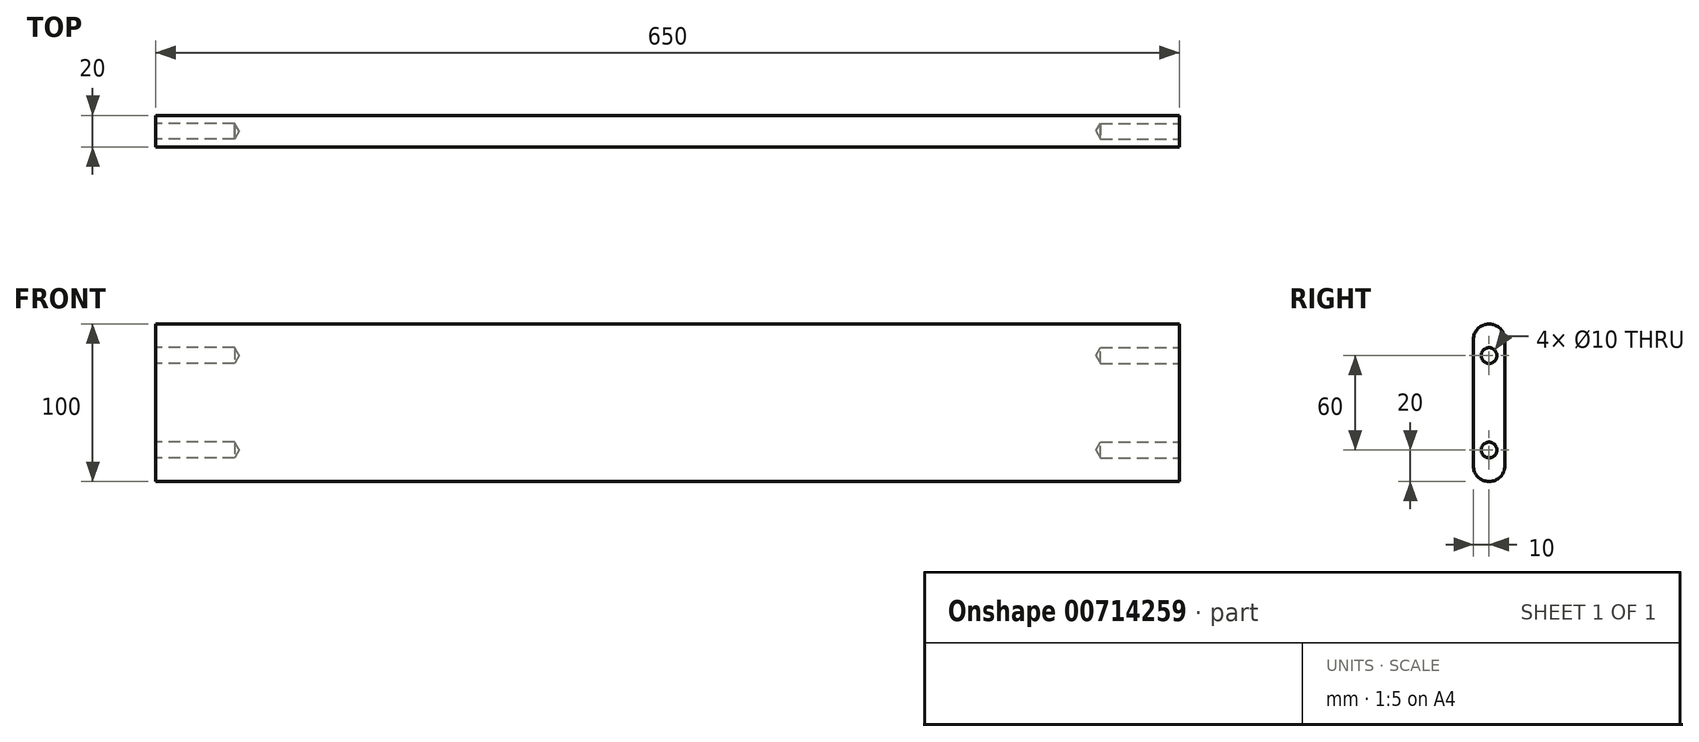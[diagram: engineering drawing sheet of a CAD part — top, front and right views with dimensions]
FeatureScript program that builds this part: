
annotation { "Feature Type Name" : "Feature", "Feature Type Description" : "" }
export const myFeature = defineFeature(function(context is Context, id is Id, definition is map)
    precondition{}
    {
        {
            var Q0;
            Q0=qCreatedBy(makeId("Front.planeOp"),FACE);
            var sketch = newSketch(context, id + "F0", { "sketchPlane" : qUnion([Q0])});
            skLineSegment(sketch, "E0.bottom", {"start": v(0, 0) * mm, "end": v(-650, 0) * mm});
            skLineSegment(sketch, "E0.top", {"start": v(0, 100) * mm, "end": v(-650, 100) * mm});
            skLineSegment(sketch, "E0.left", {"start": v(0, 0) * mm, "end": v(0, 100) * mm});
            skLineSegment(sketch, "E0.right", {"start": v(-650, 0) * mm, "end": v(-650, 100) * mm});
            skSolve(sketch);
        }
        {
            var Q0;
            Q0=makeQuery(id+"F0.imprint","IMPRINT",FACE,{"disambiguationData":[TD([[makeQuery(id+"F0.imprint","IMPRINT",EDGE,{"derivedFrom":sQuery(id+"F0.wireOp",EDGE,"E0.bottom")}),-1.0]])]});
            extrude(context, id + "F1", {"entities" : qUnion([Q0]), "depth" : 20 * mm, "offsetDistance" : 25 * mm});
        }
        {
            var Q0;
            Q0=makeQuery(id+"F1.opExtrude","CAP_EDGE",EDGE,{"disambiguationData":[OSD([sQuery(id+"F0.wireOp",EDGE,"E0.top")])],"isStart":true});
            var Q1;
            Q1=makeQuery(id+"F1.opExtrude","CAP_EDGE",EDGE,{"disambiguationData":[OSD([sQuery(id+"F0.wireOp",EDGE,"E0.top")])],"isStart":false});
            var Q2;
            Q2=makeQuery(id+"F1.opExtrude","CAP_EDGE",EDGE,{"disambiguationData":[OSD([sQuery(id+"F0.wireOp",EDGE,"E0.bottom")])],"isStart":true});
            var Q3;
            Q3=makeQuery(id+"F1.opExtrude","CAP_EDGE",EDGE,{"disambiguationData":[OSD([sQuery(id+"F0.wireOp",EDGE,"E0.bottom")])],"isStart":false});
            fillet(context, id + "F2", {"entities" : qUnion([Q0, Q1, Q2, Q3]), "radius" : 10 * mm, "tangentPropagation" : true, "allowEdgeOverflow" : false});
        }
        {
            var Q0;
            Q0=makeQuery(id+"F1.opExtrude","SWEPT_FACE",FACE,{"disambiguationData":[OSD([sQuery(id+"F0.wireOp",EDGE,"E0.right")])]});
            var sketch = newSketch(context, id + "F3", { "sketchPlane" : qUnion([Q0])});
            skCircle(sketch, "E1", {"center": v(10, 20.02) * mm, "radius": 5 * mm});
            skPoint(sketch, "E1.centerSnap0", {"position": v(10, 0) * mm});
            skCircle(sketch, "E2", {"center": v(10, 80) * mm, "radius": 5 * mm});
            skPoint(sketch, "E2.centerSnap0", {"position": v(10, 100) * mm});
            skSolve(sketch);
        }
        {
            var Q0;
            Q0=sQuery(id+"F3.wireOp",VERTEX,"E1.center");
            var Q1;
            Q1=sQuery(id+"F3.wireOp",VERTEX,"E2.center");
            var Q2;
            Q2=makeQuery(id+"F1.opExtrude","SWEPT_BODY",BODY,{"disambiguationData":[OSD([sQuery(id+"F0.wireOp",EDGE,"E0.bottom"),sQuery(id+"F0.wireOp",EDGE,"E0.top"),sQuery(id+"F0.wireOp",EDGE,"E0.left"),sQuery(id+"F0.wireOp",EDGE,"E0.right")])]});
            hole(context, id + "F4", {"style" : HoleStyle.SIMPLE, "endStyle" : HoleEndStyle.BLIND, "holeDiameter" : 10 * mm, "majorDiameter" : 5 * mm, "holeDepth" : 50 * mm, "isTappedThrough" : true, "tappedDepth" : 12 * mm, "tapClearance" : 3, "locations" : qUnion([Q0, Q1]), "scope" : qUnion([Q2])});
        }
        {
            var Q0;
            Q0=makeQuery(id+"F1.opExtrude","SWEPT_FACE",FACE,{"disambiguationData":[OSD([sQuery(id+"F0.wireOp",EDGE,"E0.left")])]});
            var sketch = newSketch(context, id + "F5", { "sketchPlane" : qUnion([Q0])});
            skCircle(sketch, "E3", {"center": v(-10, 80) * mm, "radius": 5.24 * mm});
            skPoint(sketch, "E3.centerSnap0", {"position": v(-10, 100) * mm});
            skCircle(sketch, "E4", {"center": v(-10, 20) * mm, "radius": 5.24 * mm});
            skPoint(sketch, "E4.centerSnap0", {"position": v(-10, 0) * mm});
            skSolve(sketch);
        }
        {
            var Q0;
            Q0=sQuery(id+"F5.wireOp",VERTEX,"E3.center");
            var Q1;
            Q1=sQuery(id+"F5.wireOp",VERTEX,"E4.center");
            var Q2;
            Q2=makeQuery(id+"F1.opExtrude","SWEPT_BODY",BODY,{"disambiguationData":[OSD([sQuery(id+"F0.wireOp",EDGE,"E0.bottom"),sQuery(id+"F0.wireOp",EDGE,"E0.top"),sQuery(id+"F0.wireOp",EDGE,"E0.left"),sQuery(id+"F0.wireOp",EDGE,"E0.right")])]});
            hole(context, id + "F6", {"style" : HoleStyle.SIMPLE, "endStyle" : HoleEndStyle.BLIND, "holeDiameter" : 10 * mm, "majorDiameter" : 5 * mm, "holeDepth" : 50 * mm, "isTappedThrough" : true, "tappedDepth" : 12 * mm, "tapClearance" : 3, "locations" : qUnion([Q0, Q1]), "scope" : qUnion([Q2])});
        }
    });
